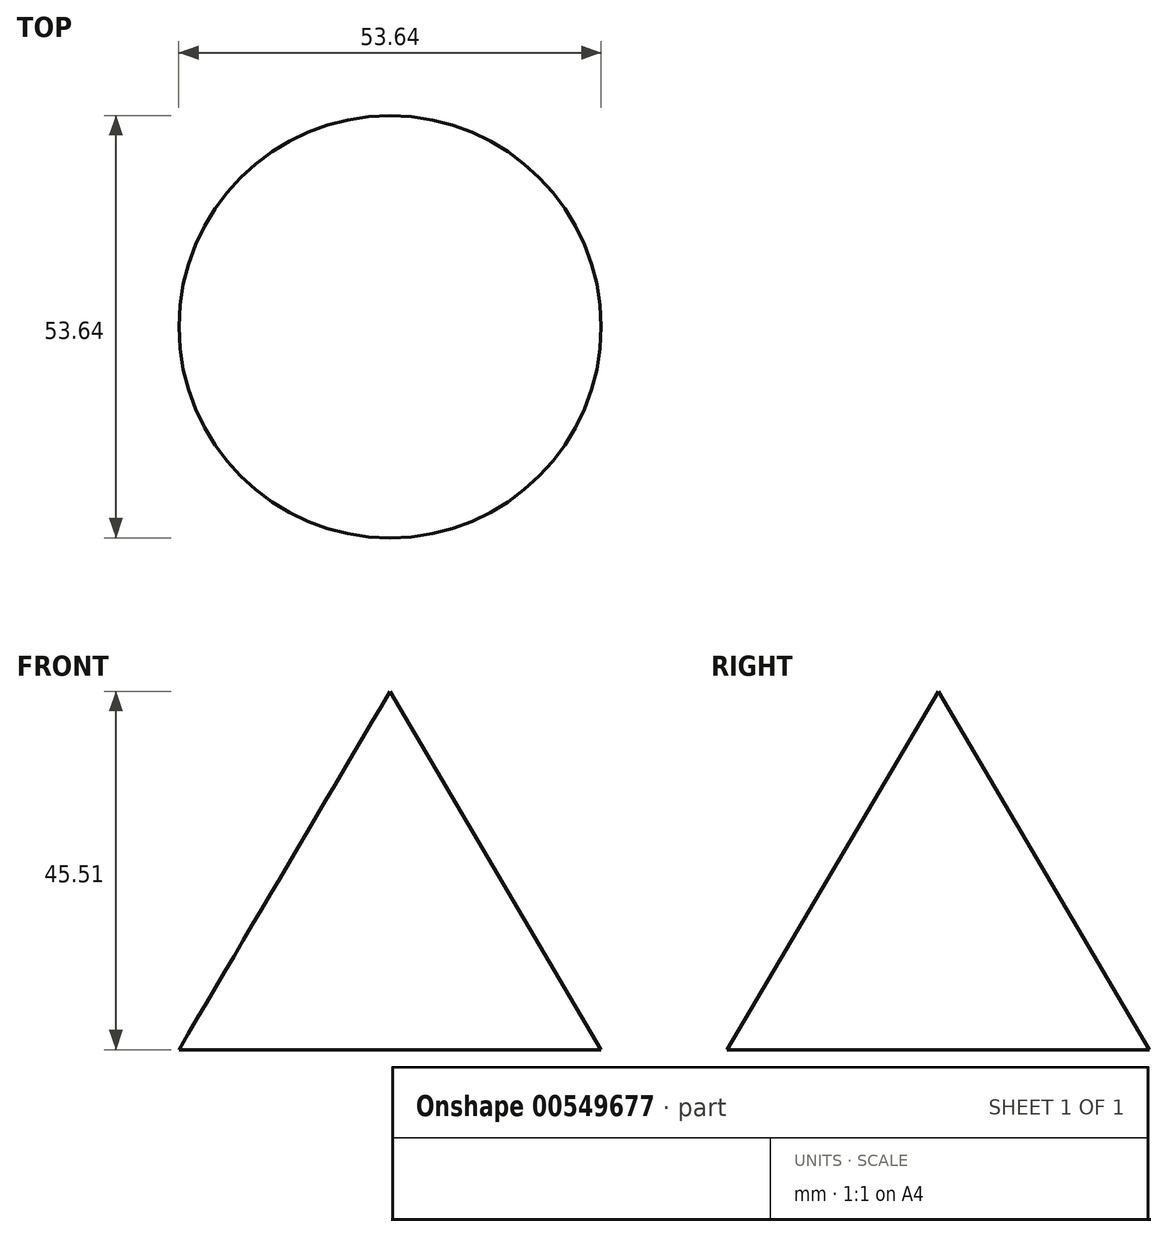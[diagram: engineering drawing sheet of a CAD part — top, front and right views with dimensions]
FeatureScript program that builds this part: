
annotation { "Feature Type Name" : "Feature", "Feature Type Description" : "" }
export const myFeature = defineFeature(function(context is Context, id is Id, definition is map)
    precondition{}
    {
        {
            var Q0;
            Q0=qCreatedBy(makeId("Front.planeOp"),FACE);
            var sketch = newSketch(context, id + "F0", { "sketchPlane" : qUnion([Q0])});
            skLineSegment(sketch, "E0", {"start": v(0, 45.51) * mm, "end": v(0, 0) * mm});
            skLineSegment(sketch, "E1", {"start": v(0, 0) * mm, "end": v(26.82, 0) * mm});
            skLineSegment(sketch, "E2", {"start": v(26.82, 0) * mm, "end": v(0, 45.51) * mm});
            skSolve(sketch);
        }
        {
            var Q0;
            Q0 = qSketchRegion(id + "F0", true);
            var Q1;
            Q1=sQuery(id+"F0.wireOp",EDGE,"E0");
            revolve(context, id + "F1", {"entities" : qUnion([Q0]), "axis" : qUnion([Q1]), "revolveType" : RevolveType.FULL});
        }
    });
